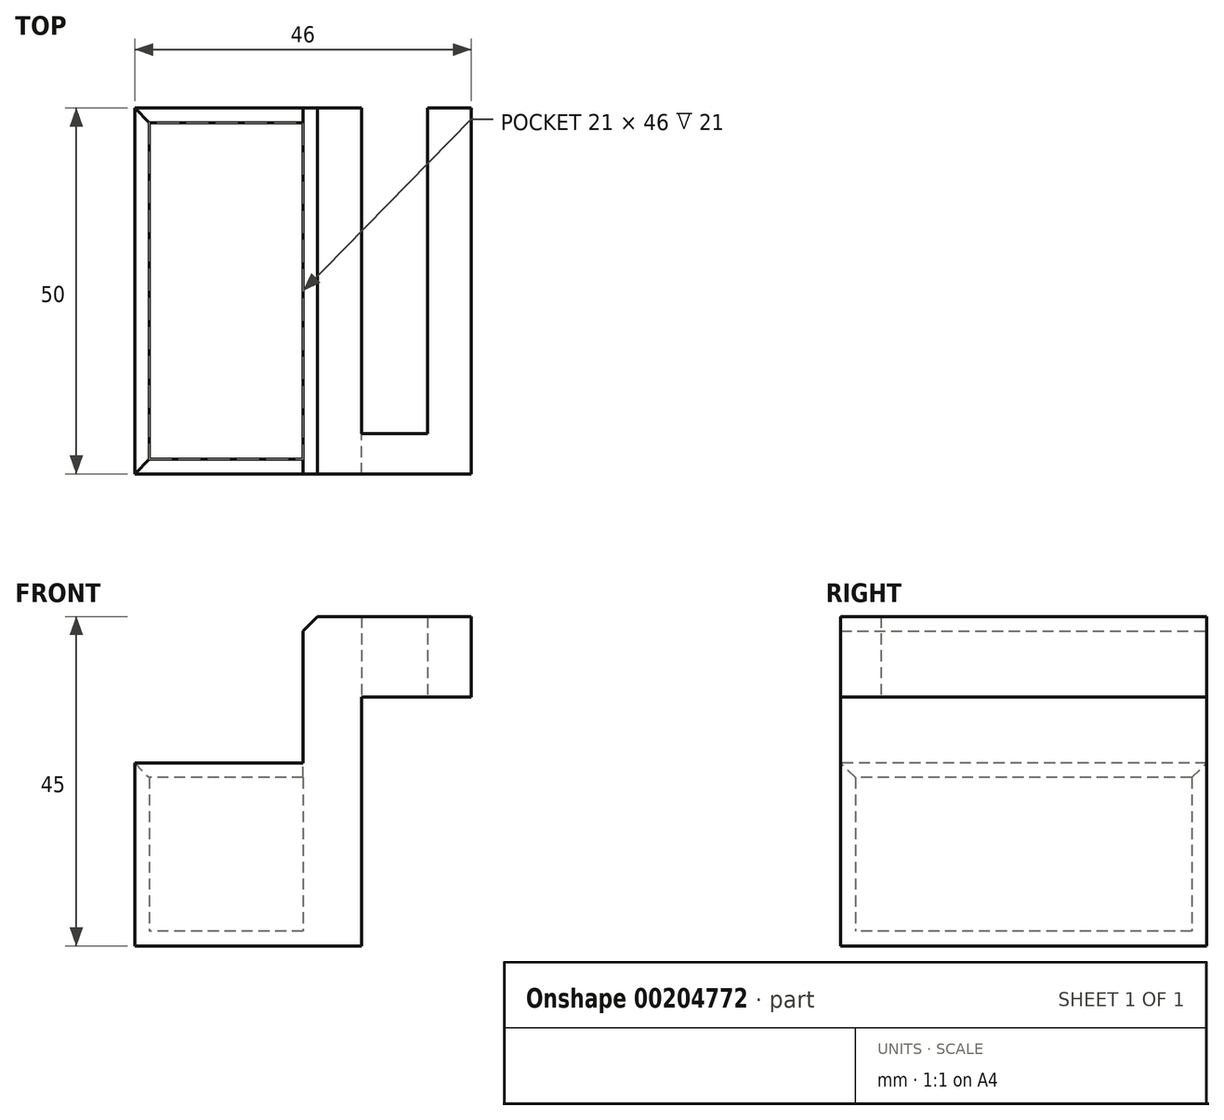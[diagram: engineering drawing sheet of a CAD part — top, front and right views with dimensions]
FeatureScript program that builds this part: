
annotation { "Feature Type Name" : "Feature", "Feature Type Description" : "" }
export const myFeature = defineFeature(function(context is Context, id is Id, definition is map)
    precondition{}
    {
        {
            var Q0;
            Q0=qCreatedBy(makeId("Top.planeOp"),FACE);
            var sketch = newSketch(context, id + "F0", { "sketchPlane" : qUnion([Q0])});
            skLineSegment(sketch, "E0.bottom", {"start": v(0, 23) * mm, "end": v(-21, 23) * mm});
            skLineSegment(sketch, "E0.top", {"start": v(0, -23) * mm, "end": v(-21, -23) * mm});
            skLineSegment(sketch, "E0.left", {"start": v(0, 23) * mm, "end": v(0, -23) * mm});
            skLineSegment(sketch, "E0.right", {"start": v(-21, 23) * mm, "end": v(-21, -23) * mm});
            skLineSegment(sketch, "E1.bottom", {"start": v(0, 25) * mm, "end": v(-23, 25) * mm});
            skLineSegment(sketch, "E1.top", {"start": v(0, -25) * mm, "end": v(-23, -25) * mm});
            skLineSegment(sketch, "E1.left", {"start": v(0, 25) * mm, "end": v(0, -25) * mm});
            skLineSegment(sketch, "E1.right", {"start": v(-23, 25) * mm, "end": v(-23, -25) * mm});
            skLineSegment(sketch, "E2.bottom", {"start": v(0, 25) * mm, "end": v(8, 25) * mm});
            skLineSegment(sketch, "E2.top", {"start": v(0, -25) * mm, "end": v(8, -25) * mm});
            skLineSegment(sketch, "E2.right", {"start": v(8, 25) * mm, "end": v(8, -25) * mm});
            skSolve(sketch);
        }
        {
            var Q0;
            Q0 = qSketchRegion(id + "F0", true);
            extrude(context, id + "F1", {"entities" : qUnion([Q0]), "depth" : 25 * mm});
        }
        {
            var Q0;
            {var subQ3=sQuery(id+"F0.wireOp",EDGE,"E2.bottom");Q0=makeQuery(id+"F0.imprint","IMPRINT",FACE,{"disambiguationData":[TD([[makeQuery(id+"F0.imprint","IMPRINT",EDGE,{"derivedFrom":subQ3}),-1.0]])]});}
            var Q1;
            {var subQ0=sQuery(id+"F0.wireOp",EDGE,"E0.bottom");Q1=makeQuery(id+"F0.imprint","IMPRINT",FACE,{"disambiguationData":[TD([[makeQuery(id+"F0.imprint","IMPRINT",EDGE,{"derivedFrom":subQ0}),1.0]])]});}
            var Q2;
            {var subQ4=sQuery(id+"F0.wireOp",EDGE,"E0.bottom");Q2=makeQuery(id+"F0.imprint","IMPRINT",FACE,{"disambiguationData":[TD([[makeQuery(id+"F0.imprint","IMPRINT",EDGE,{"derivedFrom":subQ4}),-1.0]])]});}
            extrude(context, id + "F2", {"entities" : qUnion([Q0, Q1, Q2]), "operationType" : NewBodyOperationType.ADD, "depth" : 2 * mm});
        }
        {
            var Q0;
            Q0=makeQuery(id+"F1.opExtrude","CAP_FACE",FACE,{"disambiguationData":[OSD([sQuery(id+"F0.wireOp",EDGE,"E0.bottom"),sQuery(id+"F0.wireOp",EDGE,"E0.top"),sQuery(id+"F0.wireOp",EDGE,"E0.right"),sQuery(id+"F0.wireOp",EDGE,"E1.bottom"),sQuery(id+"F0.wireOp",EDGE,"E1.top"),sQuery(id+"F0.wireOp",EDGE,"E1.right"),sQuery(id+"F0.wireOp",EDGE,"E2.bottom"),sQuery(id+"F0.wireOp",EDGE,"E2.top"),sQuery(id+"F0.wireOp",EDGE,"E1.left"),sQuery(id+"F0.wireOp",EDGE,"E2.right")])],"isStart":false});
            var sketch = newSketch(context, id + "F3", { "sketchPlane" : qUnion([Q0])});
            skLineSegment(sketch, "E3.bottom", {"start": v(0, 25) * mm, "end": v(8, 25) * mm});
            skLineSegment(sketch, "E3.top", {"start": v(0, -25) * mm, "end": v(8, -25) * mm});
            skLineSegment(sketch, "E3.left", {"start": v(0, 25) * mm, "end": v(0, -25) * mm});
            skLineSegment(sketch, "E3.right", {"start": v(8, 25) * mm, "end": v(8, -25) * mm});
            skSolve(sketch);
        }
        {
            var Q0;
            Q0 = qSketchRegion(id + "F3", true);
            extrude(context, id + "F4", {"entities" : qUnion([Q0]), "operationType" : NewBodyOperationType.ADD, "depth" : 20 * mm});
        }
        {
            var Q0;
            Q0=makeQuery(id+"F4.boolean.opBoolean","MERGE",FACE,{"derivedFrom":[makeQuery(id+"F1.opExtrude","SWEPT_FACE",FACE,{"disambiguationData":[OSD([sQuery(id+"F0.wireOp",EDGE,"E2.right")])]}),makeQuery(id+"F4.opExtrude","SWEPT_FACE",FACE,{"disambiguationData":[OSD([sQuery(id+"F3.wireOp",EDGE,"E3.right")])]})]});
            var sketch = newSketch(context, id + "F5", { "sketchPlane" : qUnion([Q0])});
            skLineSegment(sketch, "E4.bottom", {"start": v(-25, 45) * mm, "end": v(-19.5, 45) * mm});
            skLineSegment(sketch, "E4.top", {"start": v(-25, 34) * mm, "end": v(-19.5, 34) * mm});
            skLineSegment(sketch, "E4.left", {"start": v(-25, 45) * mm, "end": v(-25, 34) * mm});
            skLineSegment(sketch, "E4.right", {"start": v(-19.5, 45) * mm, "end": v(-19.5, 34) * mm});
            skSolve(sketch);
        }
        {
            var Q0;
            Q0 = qSketchRegion(id + "F5", true);
            extrude(context, id + "F6", {"entities" : qUnion([Q0]), "operationType" : NewBodyOperationType.ADD, "depth" : 15 * mm});
        }
        {
            var Q0;
            Q0=makeQuery(id+"F6.opExtrude","SWEPT_FACE",FACE,{"disambiguationData":[OSD([sQuery(id+"F5.wireOp",EDGE,"E4.right")])]});
            var sketch = newSketch(context, id + "F7", { "sketchPlane" : qUnion([Q0])});
            skLineSegment(sketch, "E5.bottom", {"start": v(-23, 45) * mm, "end": v(-17, 45) * mm});
            skLineSegment(sketch, "E5.top", {"start": v(-23, 34) * mm, "end": v(-17, 34) * mm});
            skLineSegment(sketch, "E5.left", {"start": v(-23, 45) * mm, "end": v(-23, 34) * mm});
            skLineSegment(sketch, "E5.right", {"start": v(-17, 45) * mm, "end": v(-17, 34) * mm});
            skSolve(sketch);
        }
        {
            var Q0;
            Q0 = qSketchRegion(id + "F7", true);
            var Q1;
            Q1=makeQuery(id+"F4.boolean.opBoolean","MERGE",FACE,{"derivedFrom":[makeQuery(id+"F1.opExtrude","SWEPT_FACE",FACE,{"disambiguationData":[OSD([sQuery(id+"F0.wireOp",EDGE,"E1.bottom"),sQuery(id+"F0.wireOp",EDGE,"E2.bottom")])]}),makeQuery(id+"F4.opExtrude","SWEPT_FACE",FACE,{"disambiguationData":[OSD([sQuery(id+"F3.wireOp",EDGE,"E3.bottom")])]})]});
            extrude(context, id + "F8", {"entities" : qUnion([Q0]), "operationType" : NewBodyOperationType.ADD, "endBound" : BoundingType.UP_TO_SURFACE, "endBoundEntityFace" : qUnion([Q1]), "depth" : 25 * mm});
        }
        {
            var Q0;
            Q0=makeQuery(id+"F1.opExtrude","CAP_EDGE",EDGE,{"disambiguationData":[OSD([sQuery(id+"F0.wireOp",EDGE,"E0.bottom")])],"isStart":false});
            var Q1;
            Q1=makeQuery(id+"F1.opExtrude","CAP_EDGE",EDGE,{"disambiguationData":[OSD([sQuery(id+"F0.wireOp",EDGE,"E0.right")])],"isStart":false});
            var Q2;
            Q2=makeQuery(id+"F1.opExtrude","CAP_EDGE",EDGE,{"disambiguationData":[OSD([sQuery(id+"F0.wireOp",EDGE,"E0.top")])],"isStart":false});
            var Q3;
            Q3=makeQuery(id+"F4.opExtrude","CAP_EDGE",EDGE,{"disambiguationData":[OSD([sQuery(id+"F3.wireOp",EDGE,"E3.left")])],"isStart":false});
            chamfer(context, id + "F9", {"entities" : qUnion([Q0, Q1, Q2, Q3]), "width" : 2 * mm, "tangentPropagation" : true});
        }
    });
